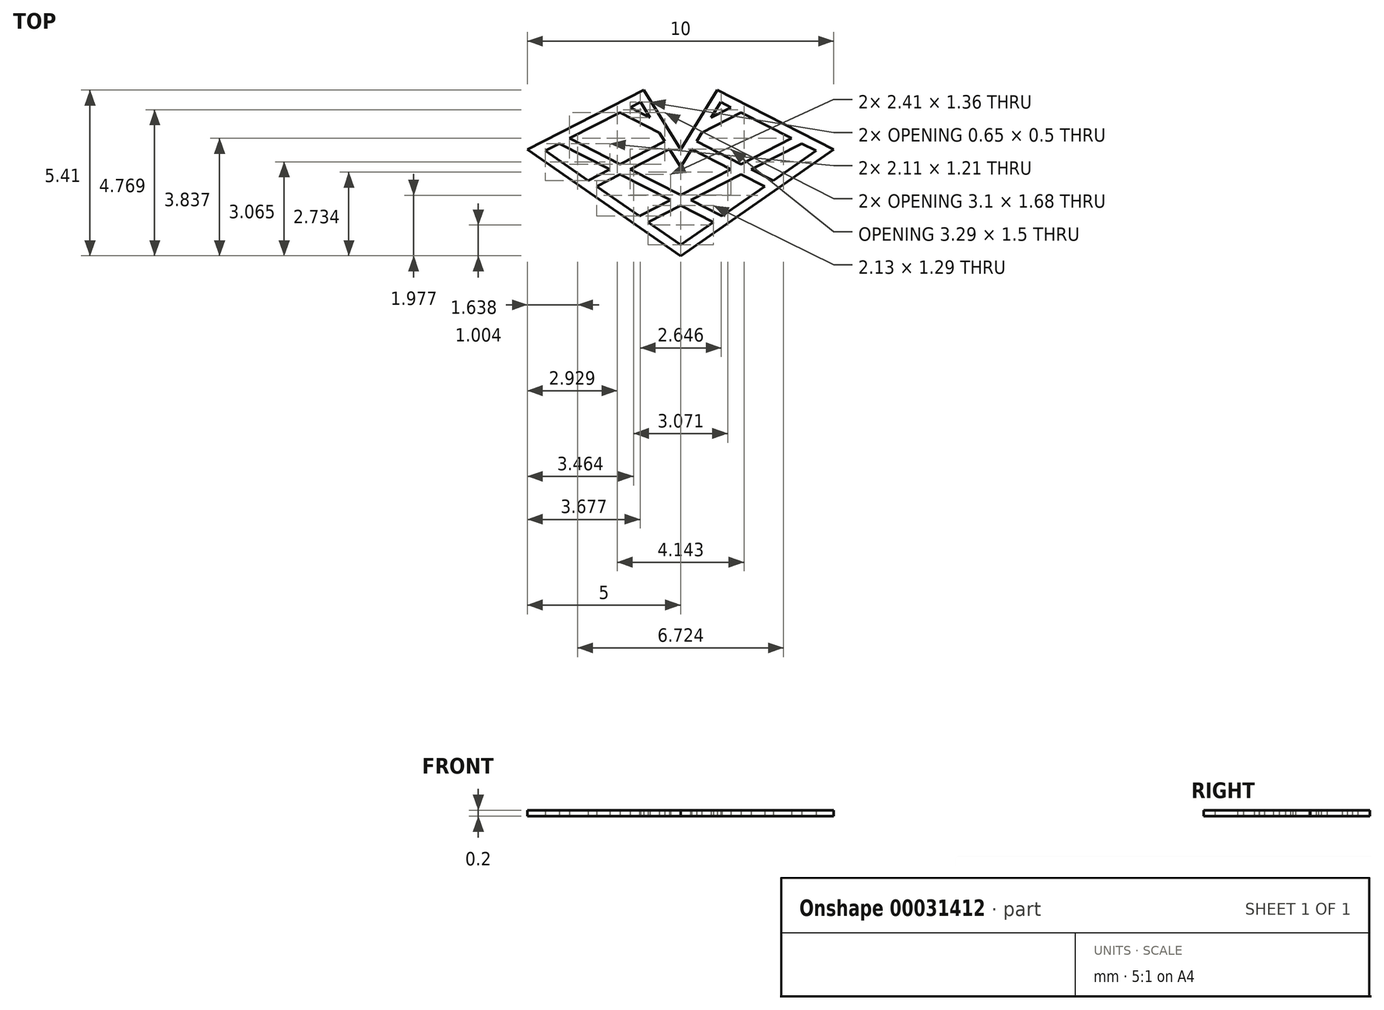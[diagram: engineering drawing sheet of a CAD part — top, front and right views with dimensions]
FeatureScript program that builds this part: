
annotation { "Feature Type Name" : "Feature", "Feature Type Description" : "" }
export const myFeature = defineFeature(function(context is Context, id is Id, definition is map)
    precondition{}
    {
        {
            var Q0;
            Q0=qCreatedBy(makeId("Top.planeOp"),FACE);
            var sketch = newSketch(context, id + "F0", { "sketchPlane" : qUnion([Q0])});
            skLineSegment(sketch, "E0", {"start": v(0, 0) * mm, "end": v(1.2, 1.94) * mm});
            skLineSegment(sketch, "E1", {"start": v(1.2, 1.94) * mm, "end": v(5, 0) * mm});
            skLineSegment(sketch, "E2", {"start": v(5, 0) * mm, "end": v(0, -3.47) * mm});
            skLineSegment(sketch, "E3.MirrorCS", {"start": v(0, 0) * mm, "end": v(-1.2, 1.94) * mm});
            skLineSegment(sketch, "E4.MirrorCS", {"start": v(-1.2, 1.94) * mm, "end": v(-5, 0) * mm});
            skLineSegment(sketch, "E5.MirrorCS", {"start": v(-5, 0) * mm, "end": v(0, -3.47) * mm});
            skLineSegment(sketch, "E6.0", {"start": v(1.3, 1.55) * mm, "end": v(1.65, 1.38) * mm});
            skLineSegment(sketch, "E7.0", {"start": v(-1.3, 1.55) * mm, "end": v(-1.65, 1.38) * mm});
            skLineSegment(sketch, "E8.0", {"start": v(-0.26, -0.16) * mm, "end": v(-0.36, 0.01) * mm});
            skLineSegment(sketch, "E9.0", {"start": v(0.26, -0.16) * mm, "end": v(0.36, 0.01) * mm});
            skLineSegment(sketch, "E10", {"start": v(-0.26, -0.16) * mm, "end": v(0, -0.57) * mm});
            skLineSegment(sketch, "E11", {"start": v(0.26, -0.16) * mm, "end": v(0, -0.57) * mm});
            skLineSegment(sketch, "E12.trimOffspring", {"start": v(4.42, -0.04) * mm, "end": v(1.35, -2.17) * mm});
            skLineSegment(sketch, "E13.trimOffspring", {"start": v(-4.42, -0.04) * mm, "end": v(-3.02, -1) * mm});
            skLineSegment(sketch, "E14.0", {"start": v(-0.63, 0.22) * mm, "end": v(-1.98, -0.48) * mm});
            skLineSegment(sketch, "E15.0", {"start": v(-0.5, -0.05) * mm, "end": v(-1.65, -0.64) * mm});
            skLineSegment(sketch, "E16.0", {"start": v(0.33, -1.65) * mm, "end": v(0.33, -1.65) * mm});
            skLineSegment(sketch, "E17", {"start": v(0.33, -1.65) * mm, "end": v(1.98, -0.81) * mm});
            skLineSegment(sketch, "E18", {"start": v(0.2, -1.39) * mm, "end": v(1.65, -0.64) * mm});
            skLineSegment(sketch, "E19", {"start": v(-0.5, -0.05) * mm, "end": v(-0.36, 0.01) * mm});
            skLineSegment(sketch, "E20", {"start": v(-0.63, 0.22) * mm, "end": v(-0.52, 0.27) * mm});
            skLineSegment(sketch, "E21.trimOffspring", {"start": v(1, 1.05) * mm, "end": v(1.65, 1.38) * mm});
            skLineSegment(sketch, "E22.trimOffspring", {"start": v(0.7, 0.55) * mm, "end": v(1.98, 1.2) * mm});
            skLineSegment(sketch, "E23.trimOffspring", {"start": v(-0.52, 0.27) * mm, "end": v(-0.7, 0.55) * mm});
            skLineSegment(sketch, "E24.trimOffspring", {"start": v(1, 1.05) * mm, "end": v(1.3, 1.55) * mm});
            skLineSegment(sketch, "E25.trimOffspring", {"start": v(3.95, 0.2) * mm, "end": v(4.42, -0.04) * mm});
            skLineSegment(sketch, "E26.trimOffspring", {"start": v(1.98, 1.2) * mm, "end": v(3.62, 0.37) * mm});
            skLineSegment(sketch, "E27.trimOffspring", {"start": v(-1.07, -2.37) * mm, "end": v(0, -3.1) * mm});
            skLineSegment(sketch, "E28.trimOffspring", {"start": v(-2.74, -1.2) * mm, "end": v(-1.35, -2.17) * mm});
            skLineSegment(sketch, "E29.0", {"start": v(1.3, -0.13) * mm, "end": v(1.98, -0.48) * mm});
            skLineSegment(sketch, "E30.0", {"start": v(1.16, -0.4) * mm, "end": v(1.65, -0.64) * mm});
            skLineSegment(sketch, "E31.0", {"start": v(0.47, -1.73) * mm, "end": v(1.35, -2.17) * mm});
            skLineSegment(sketch, "E32.0", {"start": v(0.34, -2) * mm, "end": v(1.07, -2.37) * mm});
            skLineSegment(sketch, "E33", {"start": v(1.3, -0.13) * mm, "end": v(0.52, 0.27) * mm});
            skLineSegment(sketch, "E34", {"start": v(2.94, -0.97) * mm, "end": v(3.02, -1) * mm});
            skLineSegment(sketch, "E35", {"start": v(0.47, -1.73) * mm, "end": v(0.33, -1.65) * mm});
            skLineSegment(sketch, "E36", {"start": v(0.34, -2) * mm, "end": v(0, -1.82) * mm});
            skLineSegment(sketch, "E37", {"start": v(1.16, -0.4) * mm, "end": v(0.36, 0.01) * mm});
            skLineSegment(sketch, "E38.trimOffspring", {"start": v(-1.98, 1.2) * mm, "end": v(-3.62, 0.37) * mm});
            skLineSegment(sketch, "E39.trimOffspring", {"start": v(-1, 1.05) * mm, "end": v(-1.3, 1.55) * mm});
            skLineSegment(sketch, "E40.trimOffspring", {"start": v(-1, 1.05) * mm, "end": v(-1.65, 1.38) * mm});
            skLineSegment(sketch, "E41.trimOffspring", {"start": v(-0.7, 0.55) * mm, "end": v(-1.98, 1.2) * mm});
            skLineSegment(sketch, "E42.trimOffspring", {"start": v(-3.95, 0.2) * mm, "end": v(-4.42, -0.04) * mm});
            skLineSegment(sketch, "E43.trimOffspring", {"start": v(-2.3, -0.64) * mm, "end": v(-3.02, -1) * mm});
            skLineSegment(sketch, "E44.trimOffspring", {"start": v(-2.3, -0.64) * mm, "end": v(-3.95, 0.2) * mm});
            skLineSegment(sketch, "E45.trimOffspring", {"start": v(-1.98, -0.48) * mm, "end": v(-3.62, 0.37) * mm});
            skLineSegment(sketch, "E46.trimOffspring", {"start": v(-1.98, -0.81) * mm, "end": v(-2.74, -1.2) * mm});
            skLineSegment(sketch, "E47.trimOffspring", {"start": v(-0.33, -1.65) * mm, "end": v(-1.35, -2.17) * mm});
            skLineSegment(sketch, "E48.trimOffspring", {"start": v(0, -1.49) * mm, "end": v(-1.65, -0.64) * mm});
            skLineSegment(sketch, "E49.trimOffspring", {"start": v(-0.33, -1.65) * mm, "end": v(-1.98, -0.81) * mm});
            skLineSegment(sketch, "E50.trimOffspring", {"start": v(0, -1.82) * mm, "end": v(-1.07, -2.37) * mm});
            skLineSegment(sketch, "E51", {"start": v(0.2, -1.39) * mm, "end": v(0, -1.49) * mm});
            skLineSegment(sketch, "E52.trimOffspring", {"start": v(0.52, 0.27) * mm, "end": v(0.7, 0.55) * mm});
            skLineSegment(sketch, "E53.trimOffspring", {"start": v(1.98, -0.48) * mm, "end": v(3.62, 0.37) * mm});
            skLineSegment(sketch, "E54.trimOffspring", {"start": v(1.98, -0.81) * mm, "end": v(2.8, -1.24) * mm});
            skLineSegment(sketch, "E55.trimOffspring", {"start": v(2.3, -0.64) * mm, "end": v(2.94, -0.97) * mm});
            skLineSegment(sketch, "E56.trimOffspring", {"start": v(2.3, -0.64) * mm, "end": v(3.95, 0.2) * mm});
            skLineSegment(sketch, "E57.trimOffspring", {"start": v(1.07, -2.37) * mm, "end": v(0, -3.1) * mm});
            skSolve(sketch);
        }
        {
            var Q0;
            Q0 = qSketchRegion(id + "F0", true);
            var Q1;
            Q1=makeQuery(id+"F0.imprint","IMPRINT",FACE,{"disambiguationData":[TD([[makeQuery(id+"F0.imprint","IMPRINT",EDGE,{"derivedFrom":sQuery(id+"F0.wireOp",EDGE,"E0")}),-1.0]])]});
            extrude(context, id + "F1", {"entities" : qUnion([Q0, Q1]), "depth" : .2 * mm});
        }
    });
